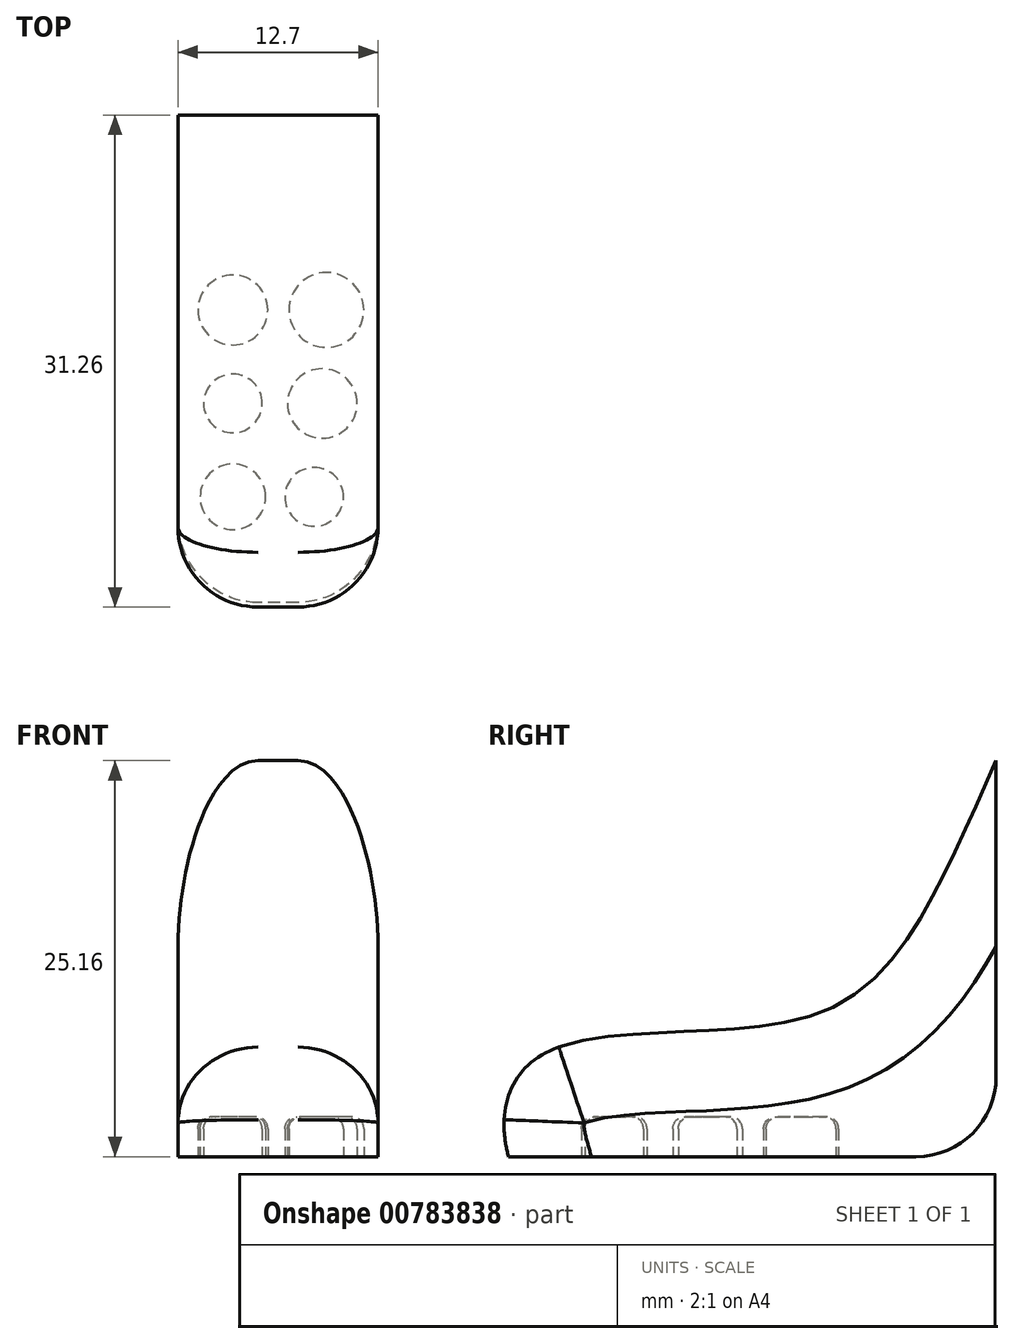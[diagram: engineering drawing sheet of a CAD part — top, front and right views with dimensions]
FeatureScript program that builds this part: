
annotation { "Feature Type Name" : "Feature", "Feature Type Description" : "" }
export const myFeature = defineFeature(function(context is Context, id is Id, definition is map)
    precondition{}
    {
        {
            var Q0;
            Q0=qCreatedBy(makeId("Right.planeOp"),FACE);
            var sketch = newSketch(context, id + "F0", { "sketchPlane" : qUnion([Q0])});
            skFitSpline(sketch, "E0", {"points": [v(-26.71, 0) * mm, v(-24.4, 6.58) * mm, v(-7.61, 8.9) * mm, v(0, 16.13) * mm, v(4.26, 25.16) * mm], "startDerivative": vector(-10.88, 40.31) * mm, "endDerivative": vector(16.63, 37.66) * mm});
            skLineSegment(sketch, "E1", {"start": v(4.26, 25.16) * mm, "end": v(4.26, 0) * mm});
            skLineSegment(sketch, "E2", {"start": v(4.26, 0) * mm, "end": v(-26.71, 0) * mm});
            skSolve(sketch);
        }
        {
            var Q0;
            Q0=makeQuery(id+"F0.imprint","IMPRINT",FACE,{"disambiguationData":[TD([[makeQuery(id+"F0.imprint","IMPRINT",EDGE,{"derivedFrom":sQuery(id+"F0.wireOp",EDGE,"E0")}),-1.0]])]});
            extrude(context, id + "F1", {"entities" : qUnion([Q0]), "depth" : 12.7 * mm, "offsetDistance" : 25.4 * mm});
        }
        {
            var Q0;
            Q0=makeQuery(id+"F1.opExtrude","CAP_EDGE",EDGE,{"disambiguationData":[OSD([sQuery(id+"F0.wireOp",EDGE,"E0")])],"isStart":true});
            var Q1;
            Q1=makeQuery(id+"F1.opExtrude","CAP_EDGE",EDGE,{"disambiguationData":[OSD([sQuery(id+"F0.wireOp",EDGE,"E0")])],"isStart":false});
            fillet(context, id + "F2", {"entities" : qUnion([Q0, Q1]), "radius" : 5.08 * mm, "tangentPropagation" : true, "allowEdgeOverflow" : false});
        }
        {
            var Q0;
            Q0=qCreatedBy(makeId("Top.planeOp"),FACE);
            var sketch = newSketch(context, id + "F3", { "sketchPlane" : qUnion([Q0])});
            skCircle(sketch, "E3", {"center": v(3.48, -20) * mm, "radius": 2.08 * mm});
            skCircle(sketch, "E4", {"center": v(8.65, -20) * mm, "radius": 1.86 * mm});
            skCircle(sketch, "E5", {"center": v(3.48, -14.07) * mm, "radius": 1.86 * mm});
            skCircle(sketch, "E6", {"center": v(9.16, -14.07) * mm, "radius": 2.2 * mm});
            skCircle(sketch, "E7", {"center": v(3.48, -8.13) * mm, "radius": 2.22 * mm});
            skCircle(sketch, "E8", {"center": v(9.42, -8.13) * mm, "radius": 2.38 * mm});
            skSolve(sketch);
        }
        {
            var Q0;
            Q0 = qSketchRegion(id + "F3", true);
            extrude(context, id + "F4", {"entities" : qUnion([Q0]), "operationType" : NewBodyOperationType.REMOVE, "depth" : 2.54 * mm, "offsetDistance" : 25.4 * mm});
        }
        {
            var Q0;
            Q0=makeQuery(id+"F4.boolean.opBoolean","COPY",EDGE,{"derivedFrom":makeQuery(id+"F4.opExtrude","CAP_EDGE",EDGE,{"disambiguationData":[OSD([sQuery(id+"F3.wireOp",EDGE,"E8")])],"isStart":false})});
            fillet(context, id + "F5", {"entities" : qUnion([Q0]), "radius" : 0.76 * mm, "tangentPropagation" : true, "allowEdgeOverflow" : false});
        }
        {
            var Q0;
            Q0=makeQuery(id+"F4.boolean.opBoolean","COPY",EDGE,{"derivedFrom":makeQuery(id+"F4.opExtrude","CAP_EDGE",EDGE,{"disambiguationData":[OSD([sQuery(id+"F3.wireOp",EDGE,"E7")])],"isStart":false})});
            var Q1;
            Q1=makeQuery(id+"F4.boolean.opBoolean","COPY",EDGE,{"derivedFrom":makeQuery(id+"F4.opExtrude","CAP_EDGE",EDGE,{"disambiguationData":[OSD([sQuery(id+"F3.wireOp",EDGE,"E5")])],"isStart":false})});
            var Q2;
            Q2=makeQuery(id+"F4.boolean.opBoolean","COPY",EDGE,{"derivedFrom":makeQuery(id+"F4.opExtrude","CAP_EDGE",EDGE,{"disambiguationData":[OSD([sQuery(id+"F3.wireOp",EDGE,"E3")])],"isStart":false})});
            var Q3;
            Q3=makeQuery(id+"F4.boolean.opBoolean","COPY",EDGE,{"derivedFrom":makeQuery(id+"F4.opExtrude","CAP_EDGE",EDGE,{"disambiguationData":[OSD([sQuery(id+"F3.wireOp",EDGE,"E6")])],"isStart":false})});
            var Q4;
            Q4=makeQuery(id+"F4.boolean.opBoolean","COPY",EDGE,{"derivedFrom":makeQuery(id+"F4.opExtrude","CAP_EDGE",EDGE,{"disambiguationData":[OSD([sQuery(id+"F3.wireOp",EDGE,"E4")])],"isStart":false})});
            fillet(context, id + "F6", {"entities" : qUnion([Q0, Q1, Q2, Q3, Q4]), "radius" : 0.76 * mm, "tangentPropagation" : true, "allowEdgeOverflow" : false});
        }
        {
            var Q0;
            Q0=makeQuery(id+"F1.opExtrude","SWEPT_EDGE",EDGE,{"disambiguationData":[OSD([sQuery(id+"F0.wireOp",EDGE,"E1"),sQuery(id+"F0.wireOp",EDGE,"E2")])]});
            fillet(context, id + "F7", {"entities" : qUnion([Q0]), "radius" : 5.08 * mm, "tangentPropagation" : true, "allowEdgeOverflow" : false});
        }
    });
